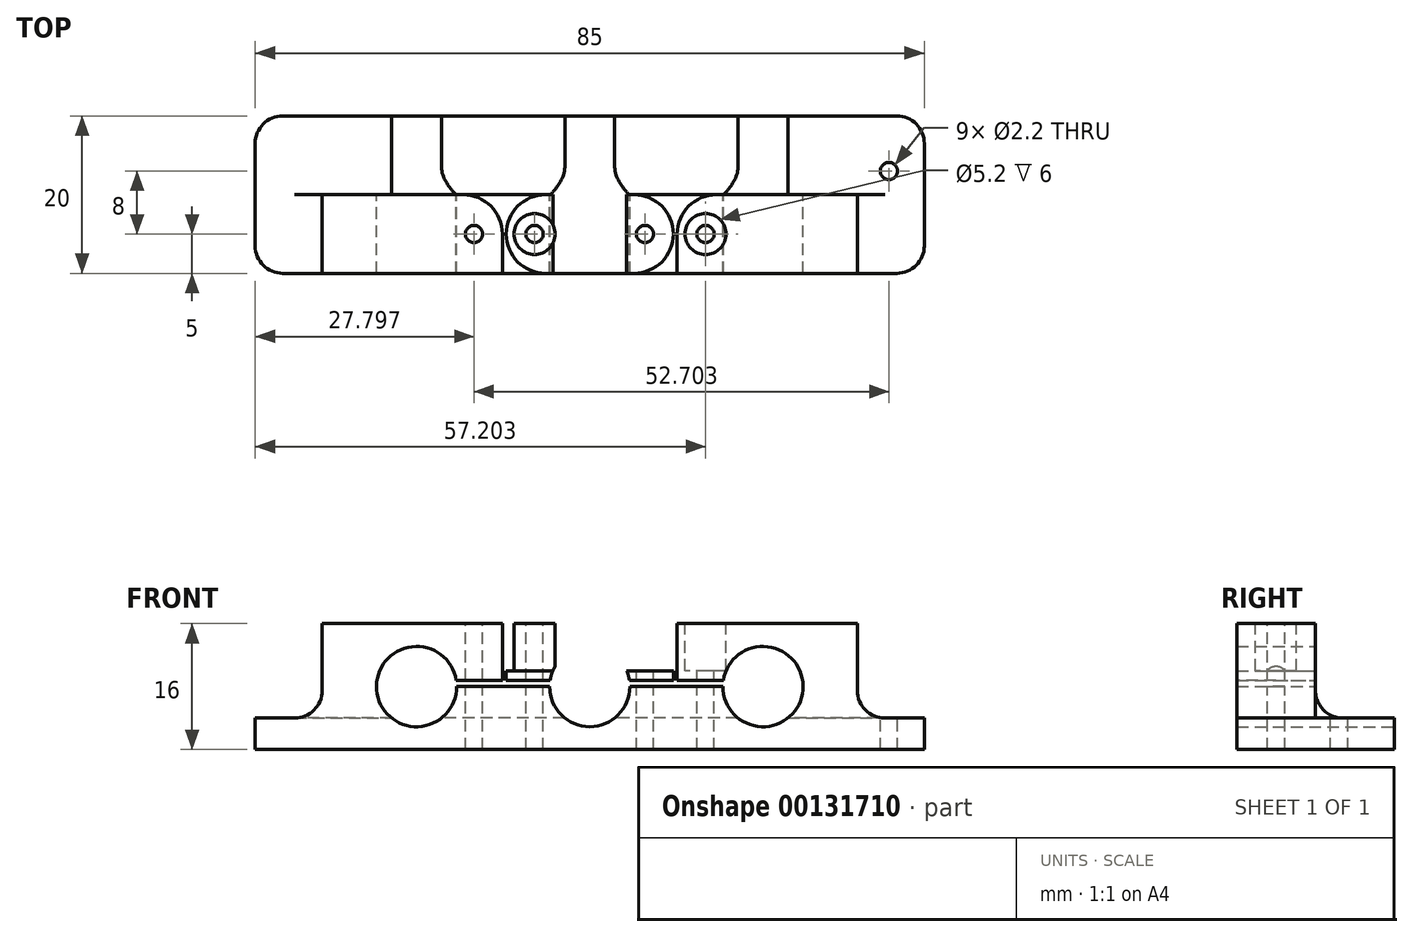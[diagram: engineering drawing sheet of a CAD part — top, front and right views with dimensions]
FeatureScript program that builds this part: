
annotation { "Feature Type Name" : "Feature", "Feature Type Description" : "" }
export const myFeature = defineFeature(function(context is Context, id is Id, definition is map)
    precondition{}
    {
        {
            var Q0;
            Q0=qCreatedBy(makeId("Front.planeOp"),FACE);
            var sketch = newSketch(context, id + "F0", { "sketchPlane" : qUnion([Q0])});
            skLineSegment(sketch, "E0.bottom", {"start": v(42.5, 8) * mm, "end": v(-42.5, 8) * mm});
            skLineSegment(sketch, "E0.top", {"start": v(42.5, -8) * mm, "end": v(-42.5, -8) * mm});
            skLineSegment(sketch, "E0.left", {"start": v(42.5, 8) * mm, "end": v(42.5, -8) * mm});
            skLineSegment(sketch, "E0.right", {"start": v(-42.5, 8) * mm, "end": v(-42.5, -8) * mm});
            skPoint(sketch, "E0.middle", {"position": v(0, 0) * mm});
            skCircle(sketch, "E1", {"center": v(0, 0) * mm, "radius": 5.1 * mm});
            skCircle(sketch, "E2", {"center": v(22, 0) * mm, "radius": 5.1 * mm});
            skCircle(sketch, "E3", {"center": v(-22, 0) * mm, "radius": 5.1 * mm});
            skSolve(sketch);
        }
        {
            var Q0;
            Q0 = qSketchRegion(id + "F0", true);
            extrude(context, id + "F1", {"entities" : qUnion([Q0]), "depth" : 20 * mm});
        }
        {
            var Q0;
            Q0=makeQuery(id+"F1.opExtrude","SWEPT_FACE",FACE,{"disambiguationData":[OSD([sQuery(id+"F0.wireOp",EDGE,"E0.bottom")])]});
            var sketch = newSketch(context, id + "F2", { "sketchPlane" : qUnion([Q0])});
            skLineSegment(sketch, "E4.bottom", {"start": v(42.5, 0) * mm, "end": v(34, 0) * mm});
            skLineSegment(sketch, "E4.top", {"start": v(42.5, -20) * mm, "end": v(34, -20) * mm});
            skLineSegment(sketch, "E4.left", {"start": v(42.5, 0) * mm, "end": v(42.5, -20) * mm});
            skLineSegment(sketch, "E4.right", {"start": v(34, 0) * mm, "end": v(34, -20) * mm});
            skLineSegment(sketch, "E5.MirrorCS", {"start": v(-34, 0) * mm, "end": v(-34, -20) * mm});
            skLineSegment(sketch, "E6.MirrorCS", {"start": v(-42.5, 0) * mm, "end": v(-42.5, -20) * mm});
            skLineSegment(sketch, "E7.MirrorCS", {"start": v(-42.5, 0) * mm, "end": v(-34, 0) * mm});
            skLineSegment(sketch, "E8.MirrorCS", {"start": v(-42.5, -20) * mm, "end": v(-34, -20) * mm});
            skLineSegment(sketch, "E9.bottom", {"start": v(-34, 0) * mm, "end": v(34, 0) * mm});
            skLineSegment(sketch, "E9.top", {"start": v(-34, -10) * mm, "end": v(34, -10) * mm});
            skLineSegment(sketch, "E9.left", {"start": v(-34, 0) * mm, "end": v(-34, -10) * mm});
            skLineSegment(sketch, "E9.right", {"start": v(34, 0) * mm, "end": v(34, -10) * mm});
            skSolve(sketch);
        }
        {
            var Q0;
            Q0 = qSketchRegion(id + "F2", true);
            extrude(context, id + "F3", {"entities" : qUnion([Q0]), "operationType" : NewBodyOperationType.REMOVE, "oppositeDirection" : true, "depth" : 12 * mm});
        }
        {
            var Q0;
            Q0=makeQuery(id+"F1.opExtrude","CAP_FACE",FACE,{"disambiguationData":[OSD([sQuery(id+"F0.wireOp",EDGE,"E0.bottom"),sQuery(id+"F0.wireOp",EDGE,"E0.top"),sQuery(id+"F0.wireOp",EDGE,"E0.left"),sQuery(id+"F0.wireOp",EDGE,"E0.right"),sQuery(id+"F0.wireOp",EDGE,"E1"),sQuery(id+"F0.wireOp",EDGE,"E2"),sQuery(id+"F0.wireOp",EDGE,"E3")])],"isStart":false});
            var sketch = newSketch(context, id + "F4", { "sketchPlane" : qUnion([Q0])});
            skLineSegment(sketch, "E10.bottom", {"start": v(-17.62, 0.8) * mm, "end": v(-3.6, 0.8) * mm});
            skLineSegment(sketch, "E10.top", {"start": v(-17.62, 0) * mm, "end": v(-3.6, 0) * mm});
            skLineSegment(sketch, "E10.left", {"start": v(-17.62, 0.8) * mm, "end": v(-17.62, 0) * mm});
            skLineSegment(sketch, "E10.right", {"start": v(-3.6, 0.8) * mm, "end": v(-3.6, 0) * mm});
            skLineSegment(sketch, "E11.bottom", {"start": v(4.21, 0) * mm, "end": v(21.75, 0) * mm});
            skLineSegment(sketch, "E11.top", {"start": v(4.21, 0.8) * mm, "end": v(21.75, 0.8) * mm});
            skLineSegment(sketch, "E11.left", {"start": v(4.21, 0) * mm, "end": v(4.21, 0.8) * mm});
            skLineSegment(sketch, "E11.right", {"start": v(21.75, 0) * mm, "end": v(21.75, 0.8) * mm});
            skPoint(sketch, "E12.oppositeSnap0", {"position": v(-10.61, 0.8) * mm});
            skLineSegment(sketch, "E12.bottom", {"start": v(-11.1, 0.8) * mm, "end": v(-10.61, 0.8) * mm});
            skLineSegment(sketch, "E12.top", {"start": v(-11.1, 8) * mm, "end": v(-10.61, 8) * mm});
            skLineSegment(sketch, "E12.left", {"start": v(-11.1, 0.8) * mm, "end": v(-11.1, 8) * mm});
            skLineSegment(sketch, "E12.right", {"start": v(-10.61, 0.8) * mm, "end": v(-10.61, 8) * mm});
            skLineSegment(sketch, "E13.MirrorCS", {"start": v(11.1, 0.8) * mm, "end": v(10.61, 0.8) * mm});
            skLineSegment(sketch, "E14.MirrorCS", {"start": v(11.1, 8) * mm, "end": v(10.61, 8) * mm});
            skPoint(sketch, "E15.MirrorP", {"position": v(10.61, 0.8) * mm});
            skLineSegment(sketch, "E16.MirrorCS", {"start": v(11.1, 0.8) * mm, "end": v(11.1, 8) * mm});
            skLineSegment(sketch, "E17.MirrorCS", {"start": v(10.61, 0.8) * mm, "end": v(10.61, 8) * mm});
            skSolve(sketch);
        }
        {
            var Q0;
            Q0 = qSketchRegion(id + "F4", true);
            extrude(context, id + "F5", {"entities" : qUnion([Q0]), "operationType" : NewBodyOperationType.REMOVE, "oppositeDirection" : true, "depth" : 25 * mm});
        }
        {
            var Q0;
            Q0=makeQuery(id+"F3.boolean.opBoolean","COPY",EDGE,{"derivedFrom":makeQuery(id+"F3.opExtrude","CAP_EDGE",EDGE,{"disambiguationData":[OSD([sQuery(id+"F2.wireOp",EDGE,"E5.MirrorCS")])],"isStart":true})});
            var Q1;
            Q1=makeQuery(id+"F3.boolean.opBoolean","COPY",EDGE,{"derivedFrom":makeQuery(id+"F3.opExtrude","CAP_EDGE",EDGE,{"disambiguationData":[OSD([sQuery(id+"F2.wireOp",EDGE,"E4.right")])],"isStart":true})});
            var Q2;
            Q2=makeQuery(id+"F3.boolean.opBoolean","COPY",EDGE,{"derivedFrom":makeQuery(id+"F3.opExtrude","CAP_EDGE",EDGE,{"disambiguationData":[OSD([sQuery(id+"F2.wireOp",EDGE,"E5.MirrorCS")])],"isStart":false})});
            var Q3;
            Q3=makeQuery(id+"F3.boolean.opBoolean","COPY",EDGE,{"derivedFrom":makeQuery(id+"F3.opExtrude","CAP_EDGE",EDGE,{"disambiguationData":[OSD([sQuery(id+"F2.wireOp",EDGE,"E4.right")])],"isStart":false})});
            var Q4;
            Q4=makeQuery(id+"F1.opExtrude","CAP_EDGE",EDGE,{"disambiguationData":[OSD([sQuery(id+"F0.wireOp",EDGE,"E0.right")])],"isStart":false});
            var Q5;
            Q5=makeQuery(id+"F1.opExtrude","CAP_EDGE",EDGE,{"disambiguationData":[OSD([sQuery(id+"F0.wireOp",EDGE,"E0.right")])],"isStart":true});
            var Q6;
            Q6=makeQuery(id+"F1.opExtrude","CAP_EDGE",EDGE,{"disambiguationData":[OSD([sQuery(id+"F0.wireOp",EDGE,"E0.left")])],"isStart":false});
            var Q7;
            Q7=makeQuery(id+"F1.opExtrude","CAP_EDGE",EDGE,{"disambiguationData":[OSD([sQuery(id+"F0.wireOp",EDGE,"E0.left")])],"isStart":true});
            var Q8;
            {var subQ0=sQuery(id+"F2.wireOp",EDGE,"E9.top");Q8=makeQuery(id+"F3.boolean.opBoolean","COPY",EDGE,{"disambiguationData":[TD([makeQuery(id+"F1.opExtrude","SWEPT_FACE",FACE,{"disambiguationData":[OSD([sQuery(id+"F0.wireOp",EDGE,"E1")])]}),makeQuery(id+"F1.opExtrude","SWEPT_FACE",FACE,{"disambiguationData":[OSD([sQuery(id+"F0.wireOp",EDGE,"E2")])]}),makeQuery(id+"F3.opExtrude","CAP_FACE",FACE,{"disambiguationData":[OSD([sQuery(id+"F2.wireOp",EDGE,"E4.bottom"),sQuery(id+"F2.wireOp",EDGE,"E4.top"),sQuery(id+"F2.wireOp",EDGE,"E4.left"),sQuery(id+"F2.wireOp",EDGE,"E4.right"),sQuery(id+"F2.wireOp",EDGE,"E5.MirrorCS"),sQuery(id+"F2.wireOp",EDGE,"E6.MirrorCS"),sQuery(id+"F2.wireOp",EDGE,"E7.MirrorCS"),sQuery(id+"F2.wireOp",EDGE,"E8.MirrorCS"),sQuery(id+"F2.wireOp",EDGE,"E9.bottom"),subQ0])],"isStart":false}),makeQuery(id+"F3.opExtrude","SWEPT_FACE",FACE,{"disambiguationData":[OSD([subQ0])]})])],"derivedFrom":makeQuery(id+"F3.opExtrude","CAP_EDGE",EDGE,{"disambiguationData":[OSD([subQ0])],"isStart":false})});}
            var Q9;
            {var subQ0=sQuery(id+"F2.wireOp",EDGE,"E9.top");Q9=makeQuery(id+"F3.boolean.opBoolean","COPY",EDGE,{"disambiguationData":[TD([makeQuery(id+"F1.opExtrude","SWEPT_FACE",FACE,{"disambiguationData":[OSD([sQuery(id+"F0.wireOp",EDGE,"E1")])]}),makeQuery(id+"F1.opExtrude","SWEPT_FACE",FACE,{"disambiguationData":[OSD([sQuery(id+"F0.wireOp",EDGE,"E3")])]}),makeQuery(id+"F3.opExtrude","CAP_FACE",FACE,{"disambiguationData":[OSD([sQuery(id+"F2.wireOp",EDGE,"E4.bottom"),sQuery(id+"F2.wireOp",EDGE,"E4.top"),sQuery(id+"F2.wireOp",EDGE,"E4.left"),sQuery(id+"F2.wireOp",EDGE,"E4.right"),sQuery(id+"F2.wireOp",EDGE,"E5.MirrorCS"),sQuery(id+"F2.wireOp",EDGE,"E6.MirrorCS"),sQuery(id+"F2.wireOp",EDGE,"E7.MirrorCS"),sQuery(id+"F2.wireOp",EDGE,"E8.MirrorCS"),sQuery(id+"F2.wireOp",EDGE,"E9.bottom"),subQ0])],"isStart":false}),makeQuery(id+"F3.opExtrude","SWEPT_FACE",FACE,{"disambiguationData":[OSD([subQ0])]})])],"derivedFrom":makeQuery(id+"F3.opExtrude","CAP_EDGE",EDGE,{"disambiguationData":[OSD([subQ0])],"isStart":false})});}
            fillet(context, id + "F6", {"entities" : qUnion([Q0, Q1, Q2, Q3, Q4, Q5, Q6, Q7, Q8, Q9]), "radius" : 3.5 * mm, "tangentPropagation" : true, "allowEdgeOverflow" : false});
        }
        {
            var Q0;
            {var subQ0=sQuery(id+"F0.wireOp",EDGE,"E0.bottom");Q0=makeQuery(id+"F5.boolean.opBoolean","SPLIT",FACE,{"disambiguationData":[TD([makeQuery(id+"F3.boolean.opBoolean","COPY",FACE,{"derivedFrom":makeQuery(id+"F3.opExtrude","SWEPT_FACE",FACE,{"disambiguationData":[OSD([sQuery(id+"F2.wireOp",EDGE,"E5.MirrorCS")])]})})])],"derivedFrom":makeQuery(id+"F1.opExtrude","SWEPT_FACE",FACE,{"disambiguationData":[OSD([subQ0])]})});}
            var sketch = newSketch(context, id + "F7", { "sketchPlane" : qUnion([Q0])});
            skCircle(sketch, "E18", {"center": v(-7.01, -15) * mm, "radius": 1.1 * mm});
            skCircle(sketch, "E19", {"center": v(-14.7, -15) * mm, "radius": 1.1 * mm});
            skCircle(sketch, "E20", {"center": v(7.01, -15) * mm, "radius": 1.1 * mm});
            skCircle(sketch, "E21", {"center": v(14.7, -15) * mm, "radius": 1.1 * mm});
            skSolve(sketch);
        }
        {
            var Q0;
            Q0=makeQuery(id+"F7.imprint","IMPRINT",FACE,{"disambiguationData":[TD([[makeQuery(id+"F7.imprint","IMPRINT",EDGE,{"derivedFrom":sQuery(id+"F7.wireOp",EDGE,"E19")}),1.0]])]});
            var Q1;
            Q1=makeQuery(id+"F7.imprint","IMPRINT",FACE,{"disambiguationData":[TD([[makeQuery(id+"F7.imprint","IMPRINT",EDGE,{"derivedFrom":sQuery(id+"F7.wireOp",EDGE,"E18")}),1.0]])]});
            var Q2;
            Q2=makeQuery(id+"F7.imprint","IMPRINT",FACE,{"disambiguationData":[TD([[makeQuery(id+"F7.imprint","IMPRINT",EDGE,{"derivedFrom":sQuery(id+"F7.wireOp",EDGE,"E20")}),1.0]])]});
            var Q3;
            Q3=makeQuery(id+"F7.imprint","IMPRINT",FACE,{"disambiguationData":[TD([[makeQuery(id+"F7.imprint","IMPRINT",EDGE,{"derivedFrom":sQuery(id+"F7.wireOp",EDGE,"E21")}),1.0]])]});
            extrude(context, id + "F8", {"entities" : qUnion([Q0, Q1, Q2, Q3]), "operationType" : NewBodyOperationType.REMOVE, "oppositeDirection" : true, "depth" : 25 * mm});
        }
        {
            var Q0;
            Q0=makeQuery(id+"F5.boolean.opBoolean","COPY",EDGE,{"derivedFrom":makeQuery(id+"F5.opExtrude","CAP_EDGE",EDGE,{"disambiguationData":[OSD([sQuery(id+"F4.wireOp",EDGE,"E12.left")])],"isStart":true})});
            var Q1;
            Q1=makeQuery(id+"F5.boolean.opBoolean","COPY",EDGE,{"derivedFrom":makeQuery(id+"F5.opExtrude","CAP_EDGE",EDGE,{"disambiguationData":[OSD([sQuery(id+"F4.wireOp",EDGE,"E12.right")])],"isStart":true})});
            var Q2;
            Q2=makeQuery(id+"F5.boolean.opBoolean","COPY",EDGE,{"derivedFrom":makeQuery(id+"F5.opExtrude","CAP_EDGE",EDGE,{"disambiguationData":[OSD([sQuery(id+"F4.wireOp",EDGE,"E17.MirrorCS")])],"isStart":true})});
            var Q3;
            Q3=makeQuery(id+"F5.boolean.opBoolean","COPY",EDGE,{"derivedFrom":makeQuery(id+"F5.opExtrude","CAP_EDGE",EDGE,{"disambiguationData":[OSD([sQuery(id+"F4.wireOp",EDGE,"E16.MirrorCS")])],"isStart":true})});
            var Q4;
            Q4=makeQuery(id+"F5.boolean.opBoolean","INTERSECT",EDGE,{"derivedFrom":[makeQuery(id+"F3.boolean.opBoolean","COPY",FACE,{"derivedFrom":makeQuery(id+"F3.opExtrude","SWEPT_FACE",FACE,{"disambiguationData":[OSD([sQuery(id+"F2.wireOp",EDGE,"E9.top")])]})}),makeQuery(id+"F5.opExtrude","SWEPT_FACE",FACE,{"disambiguationData":[OSD([sQuery(id+"F4.wireOp",EDGE,"E16.MirrorCS")])]})]});
            var Q5;
            Q5=makeQuery(id+"F5.boolean.opBoolean","INTERSECT",EDGE,{"derivedFrom":[makeQuery(id+"F3.boolean.opBoolean","COPY",FACE,{"derivedFrom":makeQuery(id+"F3.opExtrude","SWEPT_FACE",FACE,{"disambiguationData":[OSD([sQuery(id+"F2.wireOp",EDGE,"E9.top")])]})}),makeQuery(id+"F5.opExtrude","SWEPT_FACE",FACE,{"disambiguationData":[OSD([sQuery(id+"F4.wireOp",EDGE,"E17.MirrorCS")])]})]});
            var Q6;
            Q6=makeQuery(id+"F5.boolean.opBoolean","INTERSECT",EDGE,{"derivedFrom":[makeQuery(id+"F3.boolean.opBoolean","COPY",FACE,{"derivedFrom":makeQuery(id+"F3.opExtrude","SWEPT_FACE",FACE,{"disambiguationData":[OSD([sQuery(id+"F2.wireOp",EDGE,"E9.top")])]})}),makeQuery(id+"F5.opExtrude","SWEPT_FACE",FACE,{"disambiguationData":[OSD([sQuery(id+"F4.wireOp",EDGE,"E12.right")])]})]});
            var Q7;
            Q7=makeQuery(id+"F5.boolean.opBoolean","INTERSECT",EDGE,{"derivedFrom":[makeQuery(id+"F3.boolean.opBoolean","COPY",FACE,{"derivedFrom":makeQuery(id+"F3.opExtrude","SWEPT_FACE",FACE,{"disambiguationData":[OSD([sQuery(id+"F2.wireOp",EDGE,"E9.top")])]})}),makeQuery(id+"F5.opExtrude","SWEPT_FACE",FACE,{"disambiguationData":[OSD([sQuery(id+"F4.wireOp",EDGE,"E12.left")])]})]});
            fillet(context, id + "F9", {"entities" : qUnion([Q0, Q1, Q2, Q3, Q4, Q5, Q6, Q7]), "radius" : 5 * mm, "tangentPropagation" : true, "allowEdgeOverflow" : false});
        }
        {
            var Q0;
            {var subQ0=sQuery(id+"F0.wireOp",EDGE,"E2");var subQ1=sQuery(id+"F0.wireOp",EDGE,"E0.left");var subQ2=sQuery(id+"F0.wireOp",EDGE,"E3");var subQ3=sQuery(id+"F0.wireOp",EDGE,"E1");var subQ4=sQuery(id+"F0.wireOp",EDGE,"E0.right");var subQ5=sQuery(id+"F0.wireOp",EDGE,"E0.top");var subQ6=sQuery(id+"F0.wireOp",EDGE,"E0.bottom");var subQ7=sQuery(id+"F2.wireOp",EDGE,"E4.right");var subQ8=sQuery(id+"F2.wireOp",EDGE,"E9.top");Q0=makeQuery(id+"F3.boolean.opBoolean","COPY",FACE,{"disambiguationData":[TD([makeQuery(id+"F1.opExtrude","CAP_FACE",FACE,{"disambiguationData":[OSD([subQ6,subQ5,subQ1,subQ4,subQ3,subQ0,subQ2])],"isStart":true}),makeQuery(id+"F1.opExtrude","CAP_FACE",FACE,{"disambiguationData":[OSD([subQ6,subQ5,subQ1,subQ4,subQ3,subQ0,subQ2])],"isStart":false}),makeQuery(id+"F1.opExtrude","SWEPT_FACE",FACE,{"disambiguationData":[OSD([subQ1])]}),makeQuery(id+"F1.opExtrude","SWEPT_FACE",FACE,{"disambiguationData":[OSD([subQ0])]}),makeQuery(id+"F3.opExtrude","SWEPT_FACE",FACE,{"disambiguationData":[OSD([subQ7])]}),makeQuery(id+"F3.opExtrude","SWEPT_FACE",FACE,{"disambiguationData":[OSD([subQ8])]})])],"derivedFrom":makeQuery(id+"F3.opExtrude","CAP_FACE",FACE,{"disambiguationData":[OSD([sQuery(id+"F2.wireOp",EDGE,"E4.bottom"),sQuery(id+"F2.wireOp",EDGE,"E4.top"),sQuery(id+"F2.wireOp",EDGE,"E4.left"),subQ7,sQuery(id+"F2.wireOp",EDGE,"E5.MirrorCS"),sQuery(id+"F2.wireOp",EDGE,"E6.MirrorCS"),sQuery(id+"F2.wireOp",EDGE,"E7.MirrorCS"),sQuery(id+"F2.wireOp",EDGE,"E8.MirrorCS"),sQuery(id+"F2.wireOp",EDGE,"E9.bottom"),subQ8])],"isStart":false})});}
            var sketch = newSketch(context, id + "F10", { "sketchPlane" : qUnion([Q0])});
            skCircle(sketch, "E22", {"center": v(38, -7) * mm, "radius": 1.1 * mm});
            skCircle(sketch, "E23.MirrorC", {"center": v(-38, -7) * mm, "radius": 1.1 * mm});
            skSolve(sketch);
        }
        {
            var Q0;
            Q0=makeQuery(id+"F10.imprint","IMPRINT",FACE,{"disambiguationData":[TD([[makeQuery(id+"F10.imprint","IMPRINT",EDGE,{"derivedFrom":sQuery(id+"F10.wireOp",EDGE,"E22")}),1.0]])]});
            var Q1;
            Q1=makeQuery(id+"F10.imprint","IMPRINT",FACE,{"disambiguationData":[TD([[makeQuery(id+"F10.imprint","IMPRINT",EDGE,{"derivedFrom":sQuery(id+"F10.wireOp",EDGE,"E23.MirrorC")}),-1.0]])]});
            extrude(context, id + "F11", {"entities" : qUnion([Q0, Q1]), "operationType" : NewBodyOperationType.REMOVE, "oppositeDirection" : true, "depth" : 25 * mm});
        }
        {
            var Q0;
            {var subQ0=sQuery(id+"F0.wireOp",EDGE,"E0.bottom");Q0=makeQuery(id+"F5.boolean.opBoolean","SPLIT",FACE,{"disambiguationData":[TD([makeQuery(id+"F5.opExtrude","SWEPT_FACE",FACE,{"disambiguationData":[OSD([sQuery(id+"F4.wireOp",EDGE,"E12.right")])]})])],"derivedFrom":makeQuery(id+"F1.opExtrude","SWEPT_FACE",FACE,{"disambiguationData":[OSD([subQ0])]})});}
            var sketch = newSketch(context, id + "F12", { "sketchPlane" : qUnion([Q0])});
            skCircle(sketch, "E24", {"center": v(7.01, -15) * mm, "radius": 2.6 * mm});
            skCircle(sketch, "E25", {"center": v(14.7, -15) * mm, "radius": 2.6 * mm});
            skCircle(sketch, "E26.MirrorC", {"center": v(-14.7, -15) * mm, "radius": 2.6 * mm});
            skCircle(sketch, "E27.MirrorC", {"center": v(-7.01, -15) * mm, "radius": 2.6 * mm});
            skSolve(sketch);
        }
        {
            var Q0;
            Q0=makeQuery(id+"F12.imprint","IMPRINT",FACE,{"disambiguationData":[TD([[makeQuery(id+"F12.imprint","IMPRINT",EDGE,{"derivedFrom":sQuery(id+"F12.wireOp",EDGE,"E26.MirrorC")}),-1.0]])]});
            var Q1;
            Q1=makeQuery(id+"F12.imprint","IMPRINT",FACE,{"disambiguationData":[TD([[makeQuery(id+"F12.imprint","IMPRINT",EDGE,{"derivedFrom":sQuery(id+"F12.wireOp",EDGE,"E27.MirrorC")}),-1.0]])]});
            var Q2;
            Q2=makeQuery(id+"F12.imprint","IMPRINT",FACE,{"disambiguationData":[TD([[makeQuery(id+"F12.imprint","IMPRINT",EDGE,{"derivedFrom":sQuery(id+"F12.wireOp",EDGE,"E24")}),1.0]])]});
            var Q3;
            Q3=makeQuery(id+"F12.imprint","IMPRINT",FACE,{"disambiguationData":[TD([[makeQuery(id+"F12.imprint","IMPRINT",EDGE,{"derivedFrom":sQuery(id+"F12.wireOp",EDGE,"E25")}),1.0]])]});
            extrude(context, id + "F13", {"entities" : qUnion([Q0, Q1, Q2, Q3]), "operationType" : NewBodyOperationType.REMOVE, "oppositeDirection" : true, "depth" : 6 * mm});
        }
    });
